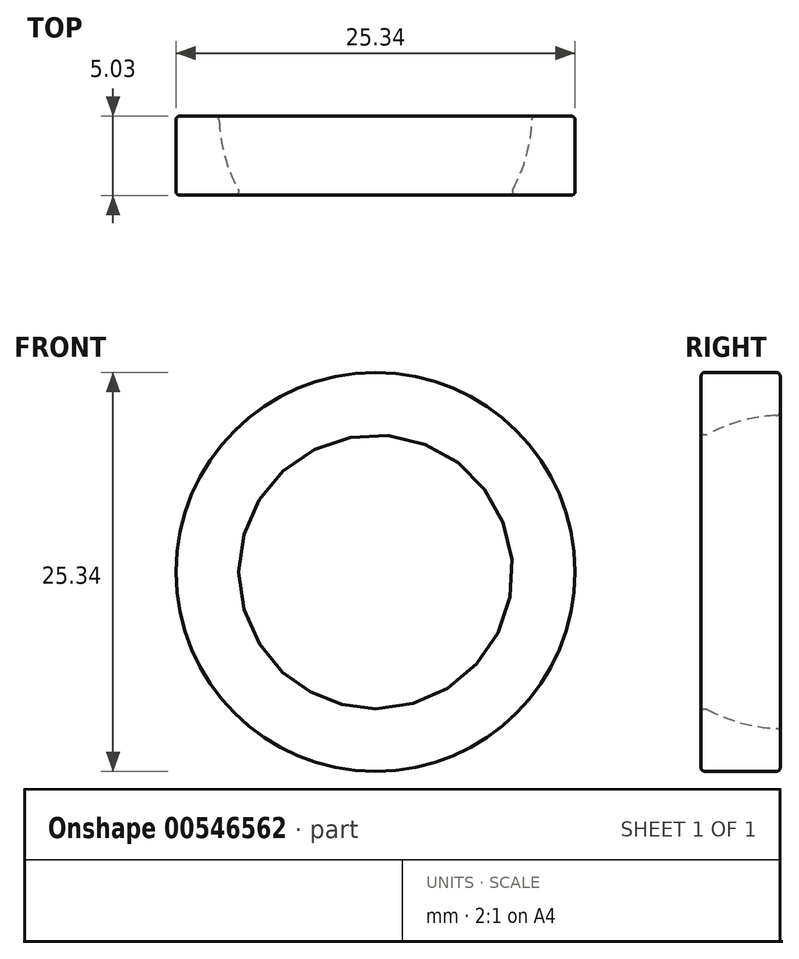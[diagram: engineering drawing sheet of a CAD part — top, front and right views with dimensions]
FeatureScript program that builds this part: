
annotation { "Feature Type Name" : "Feature", "Feature Type Description" : "" }
export const myFeature = defineFeature(function(context is Context, id is Id, definition is map)
    precondition{}
    {
        {
            var Q0;
            Q0=qCreatedBy(makeId("Front.planeOp"),FACE);
            cPlane(context, id + "F0", {"entities" : qUnion([Q0]), "cplaneType" : CPlaneType.OFFSET, "offset" : 0.13 * mm, "width" : 152.4 * mm, "height" : 152.4 * mm});
        }
        {
            var Q0;
            Q0=qCreatedBy(id+"F0.planeOp",FACE);
            var sketch = newSketch(context, id + "F1", { "sketchPlane" : qUnion([Q0])});
            skCircle(sketch, "E0", {"center": v(0, 0) * mm, "radius": 12.67 * mm});
            skSolve(sketch);
        }
        {
            var Q0;
            Q0=makeQuery(id+"F1.imprint","IMPRINT",FACE,{"disambiguationData":[TD([[makeQuery(id+"F1.imprint","IMPRINT",EDGE,{"derivedFrom":sQuery(id+"F1.wireOp",EDGE,"E0")}),1.0]])]});
            extrude(context, id + "F2", {"entities" : qUnion([Q0]), "depth" : 5.03 * mm, "offsetDistance" : 25.4 * mm});
        }
        {
            var Q0;
            Q0=qCreatedBy(makeId("Right.planeOp"),FACE);
            var sketch = newSketch(context, id + "F3", { "sketchPlane" : qUnion([Q0])});
            skLineSegment(sketch, "E1", {"start": v(0, 0) * mm, "end": v(-9.94, 0) * mm});
            skArc(sketch, "E2", {"start": v(-9.94, 0) * mm, "mid": v(0, 9.94) * mm, "end": v(9.94, 0) * mm});
            skLineSegment(sketch, "E3", {"start": v(0, 0) * mm, "end": v(9.94, 0) * mm});
            skSolve(sketch);
        }
        {
            var Q0;
            Q0=makeQuery(id+"F3.imprint","IMPRINT",FACE,{"disambiguationData":[TD([[makeQuery(id+"F3.imprint","IMPRINT",EDGE,{"derivedFrom":sQuery(id+"F3.wireOp",EDGE,"E1")}),-1.0]])]});
            var Q1;
            Q1=sQuery(id+"F3.wireOp",EDGE,"E3");
            revolve(context, id + "F4", {"operationType" : NewBodyOperationType.REMOVE, "entities" : qUnion([Q0]), "axis" : qUnion([Q1]), "revolveType" : RevolveType.FULL});
        }
        {
            var Q0;
            Q0=makeQuery(id+"F4.boolean.opBoolean","INTERSECT",EDGE,{"derivedFrom":[makeQuery(id+"F2.opExtrude","CAP_FACE",FACE,{"disambiguationData":[OSD([sQuery(id+"F1.wireOp",EDGE,"E0")])],"isStart":false}),makeQuery(id+"F4.opRevolve","SWEPT_FACE",FACE,{"disambiguationData":[OSD([sQuery(id+"F3.wireOp",EDGE,"E2")])]})]});
            var Q1;
            Q1=makeQuery(id+"F2.opExtrude","CAP_EDGE",EDGE,{"disambiguationData":[OSD([sQuery(id+"F1.wireOp",EDGE,"E0")])],"isStart":false});
            var Q2;
            Q2=makeQuery(id+"F2.opExtrude","CAP_EDGE",EDGE,{"disambiguationData":[OSD([sQuery(id+"F1.wireOp",EDGE,"E0")])],"isStart":true});
            var Q3;
            Q3=makeQuery(id+"F4.boolean.opBoolean","INTERSECT",EDGE,{"derivedFrom":[makeQuery(id+"F2.opExtrude","CAP_FACE",FACE,{"disambiguationData":[OSD([sQuery(id+"F1.wireOp",EDGE,"E0")])],"isStart":true}),makeQuery(id+"F4.opRevolve","SWEPT_FACE",FACE,{"disambiguationData":[OSD([sQuery(id+"F3.wireOp",EDGE,"E2")])]})]});
            fillet(context, id + "F5", {"entities" : qUnion([Q0, Q1, Q2, Q3]), "radius" : 0.25 * mm, "tangentPropagation" : true, "allowEdgeOverflow" : false});
        }
    });
